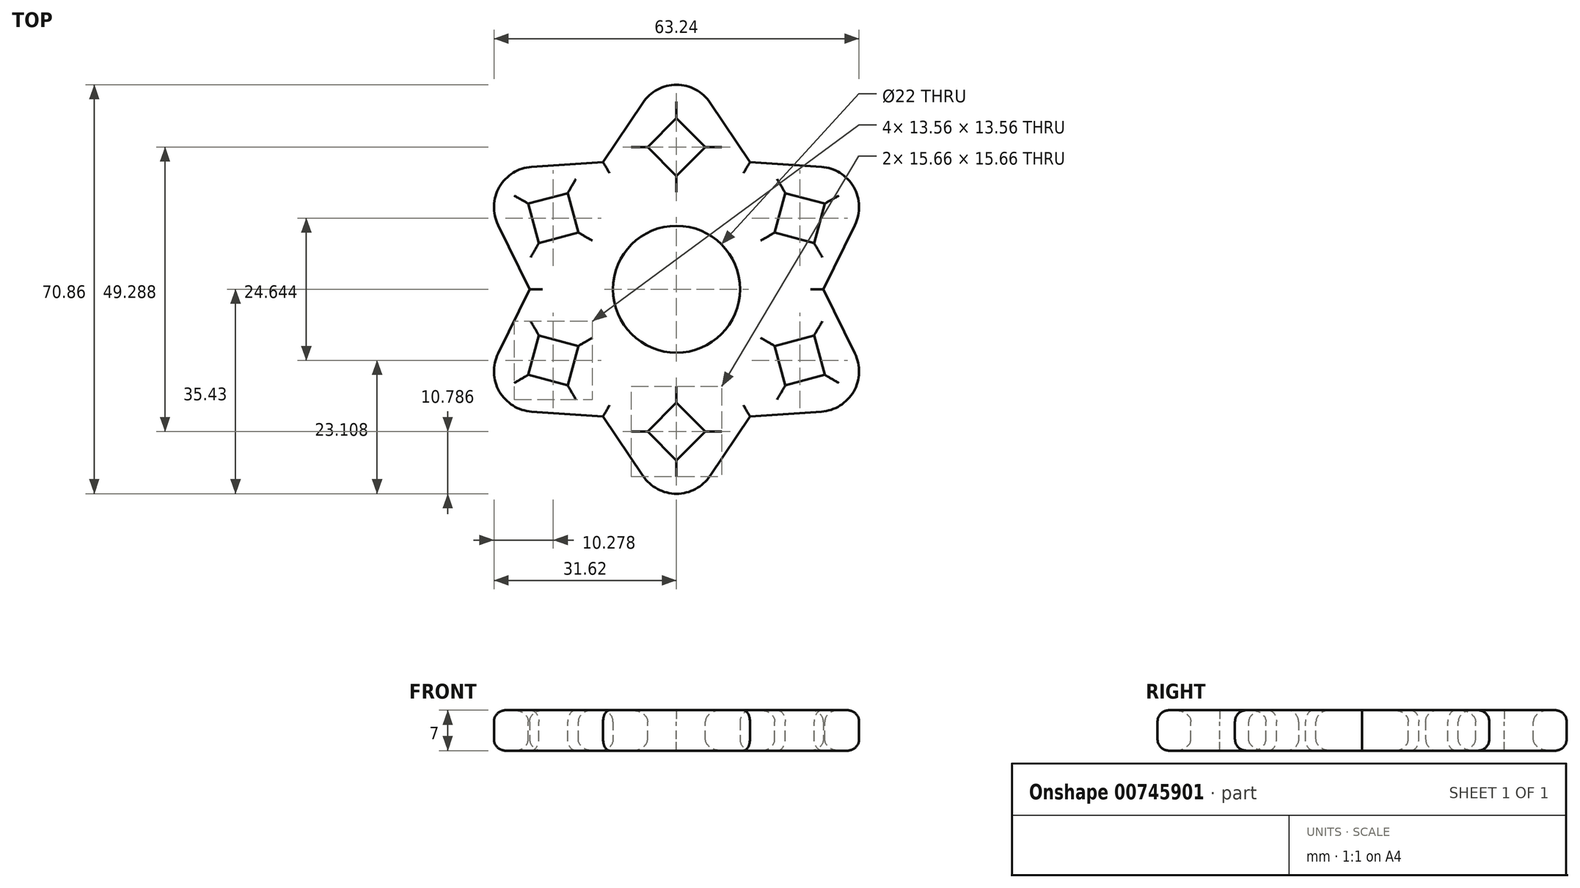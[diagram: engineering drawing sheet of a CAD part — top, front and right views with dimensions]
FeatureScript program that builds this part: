
annotation { "Feature Type Name" : "Feature", "Feature Type Description" : "" }
export const myFeature = defineFeature(function(context is Context, id is Id, definition is map)
    precondition{}
    {
        {
            var Q0;
            Q0=qCreatedBy(makeId("Top.planeOp"),FACE);
            var sketch = newSketch(context, id + "F0", { "sketchPlane" : qUnion([Q0])});
            skCircle(sketch, "E0", {"center": v(0, 0) * mm, "radius": 11 * mm});
            skLineSegment(sketch, "E1", {"start": v(0, 11) * mm, "end": v(0, 41) * mm});
            skLineSegment(sketch, "E2", {"start": v(0, 41) * mm, "end": v(16.7, 16.08) * mm});
            skLineSegment(sketch, "E3", {"start": v(16.7, 16.08) * mm, "end": v(10.48, -3.36) * mm});
            skLineSegment(sketch, "E4.MirrorCS", {"start": v(-16.7, 16.08) * mm, "end": v(-10.48, -3.36) * mm});
            skLineSegment(sketch, "E5.MirrorCS", {"start": v(0, 41) * mm, "end": v(-16.7, 16.08) * mm});
            skSolve(sketch);
        }
        {
            var Q0;
            {var subQ0=sQuery(id+"F0.wireOp",EDGE,"E4.MirrorCS");Q0=makeQuery(id+"F0.imprint","IMPRINT",FACE,{"disambiguationData":[TD([[makeQuery(id+"F0.imprint","IMPRINT",EDGE,{"derivedFrom":subQ0}),1.0]])]});}
            var Q1;
            Q1=makeQuery(id+"F0.imprint","IMPRINT",FACE,{"disambiguationData":[TD([[makeQuery(id+"F0.imprint","IMPRINT",EDGE,{"derivedFrom":sQuery(id+"F0.wireOp",EDGE,"E2")}),-1.0]])]});
            extrude(context, id + "F1", {"entities" : qUnion([Q0, Q1]), "depth" : 7 * mm, "offsetDistance" : 25 * mm});
        }
        {
            var Q0;
            Q0=makeQuery(id+"F1.opExtrude","SWEPT_EDGE",EDGE,{"disambiguationData":[OSD([sQuery(id+"F0.wireOp",EDGE,"E2"),sQuery(id+"F0.wireOp",EDGE,"E1"),sQuery(id+"F0.wireOp",EDGE,"E5.MirrorCS")])]});
            var Q1;
            Q1=makeQuery(id+"F1.opExtrude","SWEPT_EDGE",EDGE,{"disambiguationData":[OSD([sQuery(id+"F0.wireOp",EDGE,"E4.MirrorCS"),sQuery(id+"F0.wireOp",EDGE,"E5.MirrorCS")])]});
            var Q2;
            Q2=makeQuery(id+"F1.opExtrude","SWEPT_EDGE",EDGE,{"disambiguationData":[OSD([sQuery(id+"F0.wireOp",EDGE,"E2"),sQuery(id+"F0.wireOp",EDGE,"E3")])]});
            fillet(context, id + "F2", {"entities" : qUnion([Q0, Q1, Q2]), "radius" : 7 * mm, "tangentPropagation" : true, "allowEdgeOverflow" : false});
        }
        {
            var Q0;
            Q0=makeQuery(id+"F1.opExtrude","CAP_FACE",FACE,{"disambiguationData":[OSD([sQuery(id+"F0.wireOp",EDGE,"E0"),sQuery(id+"F0.wireOp",EDGE,"E2"),sQuery(id+"F0.wireOp",EDGE,"E3"),sQuery(id+"F0.wireOp",EDGE,"E4.MirrorCS"),sQuery(id+"F0.wireOp",EDGE,"E5.MirrorCS")])],"isStart":false});
            var Q1;
            Q1=makeQuery(id+"F1.opExtrude","CAP_FACE",FACE,{"disambiguationData":[OSD([sQuery(id+"F0.wireOp",EDGE,"E0"),sQuery(id+"F0.wireOp",EDGE,"E2"),sQuery(id+"F0.wireOp",EDGE,"E3"),sQuery(id+"F0.wireOp",EDGE,"E4.MirrorCS"),sQuery(id+"F0.wireOp",EDGE,"E5.MirrorCS")])],"isStart":true});
            fillet(context, id + "F3", {"entities" : qUnion([Q0, Q1]), "radius" : 2 * mm, "tangentPropagation" : true, "allowEdgeOverflow" : false});
        }
        {
            var Q0;
            Q0=makeQuery(id+"F1.opExtrude","CAP_FACE",FACE,{"disambiguationData":[OSD([sQuery(id+"F0.wireOp",EDGE,"E0"),sQuery(id+"F0.wireOp",EDGE,"E2"),sQuery(id+"F0.wireOp",EDGE,"E3"),sQuery(id+"F0.wireOp",EDGE,"E4.MirrorCS"),sQuery(id+"F0.wireOp",EDGE,"E5.MirrorCS")])],"isStart":false});
            var sketch = newSketch(context, id + "F4", { "sketchPlane" : qUnion([Q0])});
            skLineSegment(sketch, "E6", {"start": v(0, 24.64) * mm, "end": v(0, 29.64) * mm});
            skLineSegment(sketch, "E7", {"start": v(0, 24.64) * mm, "end": v(0, 19.64) * mm});
            skLineSegment(sketch, "E8", {"start": v(0, 24.64) * mm, "end": v(5, 24.64) * mm});
            skLineSegment(sketch, "E9", {"start": v(0, 24.64) * mm, "end": v(-5, 24.64) * mm});
            skLineSegment(sketch, "E10", {"start": v(0, 29.64) * mm, "end": v(-5, 24.64) * mm});
            skLineSegment(sketch, "E11", {"start": v(0, 19.64) * mm, "end": v(5, 24.64) * mm});
            skLineSegment(sketch, "E12", {"start": v(0, 29.64) * mm, "end": v(5, 24.64) * mm});
            skLineSegment(sketch, "E13", {"start": v(0, 19.64) * mm, "end": v(-5, 24.64) * mm});
            skSolve(sketch);
        }
        {
            var Q0;
            Q0=makeQuery(id+"F4.imprint","IMPRINT",FACE,{"disambiguationData":[TD([[makeQuery(id+"F4.imprint","IMPRINT",EDGE,{"derivedFrom":sQuery(id+"F4.wireOp",EDGE,"E6")}),1.0]])]});
            var Q1;
            Q1=makeQuery(id+"F4.imprint","IMPRINT",FACE,{"disambiguationData":[TD([[makeQuery(id+"F4.imprint","IMPRINT",EDGE,{"derivedFrom":sQuery(id+"F4.wireOp",EDGE,"E7")}),1.0]])]});
            var Q2;
            Q2=makeQuery(id+"F4.imprint","IMPRINT",FACE,{"disambiguationData":[TD([[makeQuery(id+"F4.imprint","IMPRINT",EDGE,{"derivedFrom":sQuery(id+"F4.wireOp",EDGE,"E6")}),-1.0]])]});
            var Q3;
            Q3=makeQuery(id+"F4.imprint","IMPRINT",FACE,{"disambiguationData":[TD([[makeQuery(id+"F4.imprint","IMPRINT",EDGE,{"derivedFrom":sQuery(id+"F4.wireOp",EDGE,"E7")}),-1.0]])]});
            extrude(context, id + "F5", {"entities" : qUnion([Q0, Q1, Q2, Q3]), "operationType" : NewBodyOperationType.REMOVE, "oppositeDirection" : true, "depth" : 25 * mm, "offsetDistance" : 25 * mm});
        }
        {
            var Q0;
            Q0=makeQuery(id+"F5.boolean.opBoolean","COPY",EDGE,{"derivedFrom":makeQuery(id+"F5.opExtrude","CAP_EDGE",EDGE,{"disambiguationData":[OSD([sQuery(id+"F4.wireOp",EDGE,"E11")])],"isStart":true})});
            var Q1;
            Q1=makeQuery(id+"F5.boolean.opBoolean","COPY",EDGE,{"derivedFrom":makeQuery(id+"F5.opExtrude","CAP_EDGE",EDGE,{"disambiguationData":[OSD([sQuery(id+"F4.wireOp",EDGE,"E12")])],"isStart":true})});
            var Q2;
            Q2=makeQuery(id+"F1.opExtrude","CAP_FACE",FACE,{"disambiguationData":[OSD([sQuery(id+"F0.wireOp",EDGE,"E0"),sQuery(id+"F0.wireOp",EDGE,"E2"),sQuery(id+"F0.wireOp",EDGE,"E3"),sQuery(id+"F0.wireOp",EDGE,"E4.MirrorCS"),sQuery(id+"F0.wireOp",EDGE,"E5.MirrorCS")])],"isStart":false});
            var Q3;
            Q3=makeQuery(id+"F5.boolean.opBoolean","COPY",EDGE,{"derivedFrom":makeQuery(id+"F5.opExtrude","CAP_EDGE",EDGE,{"disambiguationData":[OSD([sQuery(id+"F4.wireOp",EDGE,"E13")])],"isStart":true})});
            var Q4;
            Q4=makeQuery(id+"F5.boolean.opBoolean","INTERSECT",EDGE,{"derivedFrom":[makeQuery(id+"F1.opExtrude","CAP_FACE",FACE,{"disambiguationData":[OSD([sQuery(id+"F0.wireOp",EDGE,"E0"),sQuery(id+"F0.wireOp",EDGE,"E2"),sQuery(id+"F0.wireOp",EDGE,"E3"),sQuery(id+"F0.wireOp",EDGE,"E4.MirrorCS"),sQuery(id+"F0.wireOp",EDGE,"E5.MirrorCS")])],"isStart":true}),makeQuery(id+"F5.opExtrude","SWEPT_FACE",FACE,{"disambiguationData":[OSD([sQuery(id+"F4.wireOp",EDGE,"E13")])]})]});
            var Q5;
            Q5=makeQuery(id+"F5.boolean.opBoolean","INTERSECT",EDGE,{"derivedFrom":[makeQuery(id+"F1.opExtrude","CAP_FACE",FACE,{"disambiguationData":[OSD([sQuery(id+"F0.wireOp",EDGE,"E0"),sQuery(id+"F0.wireOp",EDGE,"E2"),sQuery(id+"F0.wireOp",EDGE,"E3"),sQuery(id+"F0.wireOp",EDGE,"E4.MirrorCS"),sQuery(id+"F0.wireOp",EDGE,"E5.MirrorCS")])],"isStart":true}),makeQuery(id+"F5.opExtrude","SWEPT_FACE",FACE,{"disambiguationData":[OSD([sQuery(id+"F4.wireOp",EDGE,"E12")])]})]});
            var Q6;
            Q6=makeQuery(id+"F5.boolean.opBoolean","INTERSECT",EDGE,{"derivedFrom":[makeQuery(id+"F1.opExtrude","CAP_FACE",FACE,{"disambiguationData":[OSD([sQuery(id+"F0.wireOp",EDGE,"E0"),sQuery(id+"F0.wireOp",EDGE,"E2"),sQuery(id+"F0.wireOp",EDGE,"E3"),sQuery(id+"F0.wireOp",EDGE,"E4.MirrorCS"),sQuery(id+"F0.wireOp",EDGE,"E5.MirrorCS")])],"isStart":true}),makeQuery(id+"F5.opExtrude","SWEPT_FACE",FACE,{"disambiguationData":[OSD([sQuery(id+"F4.wireOp",EDGE,"E10")])]})]});
            var Q7;
            Q7=makeQuery(id+"F5.boolean.opBoolean","INTERSECT",EDGE,{"derivedFrom":[makeQuery(id+"F1.opExtrude","CAP_FACE",FACE,{"disambiguationData":[OSD([sQuery(id+"F0.wireOp",EDGE,"E0"),sQuery(id+"F0.wireOp",EDGE,"E2"),sQuery(id+"F0.wireOp",EDGE,"E3"),sQuery(id+"F0.wireOp",EDGE,"E4.MirrorCS"),sQuery(id+"F0.wireOp",EDGE,"E5.MirrorCS")])],"isStart":true}),makeQuery(id+"F5.opExtrude","SWEPT_FACE",FACE,{"disambiguationData":[OSD([sQuery(id+"F4.wireOp",EDGE,"E11")])]})]});
            fillet(context, id + "F6", {"entities" : qUnion([Q0, Q1, Q2, Q3, Q4, Q5, Q6, Q7]), "radius" : 2 * mm, "tangentPropagation" : true, "allowEdgeOverflow" : false});
        }
        {
            var Q0;
            Q0=makeQuery(id+"F1.opExtrude","SWEPT_BODY",BODY,{"disambiguationData":[OSD([sQuery(id+"F0.wireOp",EDGE,"E0"),sQuery(id+"F0.wireOp",EDGE,"E2"),sQuery(id+"F0.wireOp",EDGE,"E3"),sQuery(id+"F0.wireOp",EDGE,"E4.MirrorCS"),sQuery(id+"F0.wireOp",EDGE,"E5.MirrorCS")])]});
            var Q1;
            Q1=sQuery(id+"F0.wireOp",EDGE,"E0");
            circularPattern(context, id + "F7", {"operationType" : NewBodyOperationType.ADD, "entities" : qUnion([Q0]), "axis" : qUnion([Q1]), "angle" : 360 * degree, "instanceCount" : 6, "oppositeDirection" : true, "equalSpace" : true});
        }
    });
